# Revit family: Combination_Tissue_Toilet_Seat_Dispenser-Bobrick-ClassicSeries-B-3091
name_source: partatom
category: Specialty Equipment
revit_build: Autodesk Revit 2014 (Build: 20130308_1515(x64)
units: mm (PartAtom-declared; Revit-internal decimal feet)

## types (1)
- B-3091
    ADA Compliant = No
    Assembly Code = C1030200
    Default Elevation = 17 7/8"
    Depth = 3 15/16"
    Description = ClassicSeries Recessed Toilet Seat-Cover Dispenser, Waste Disposal, and Toilet Tissue Dispenser
    Finish = Stainless Steel-Bobrick-Type 304-Satin
    Height = 14"
    Installation Type = Surface-Mounted
    Manufacturer = Bobrick
    Material = Stainless Steel-Bobrick-Type 304-Satin
    Model = B-3091
    Price = Prices may vary. Please consult Manufacturer Representative for most up-to-date price list.
    Revised Date = 08/15/2019
    URL = http://www.bobrick.com
    Width = 28"

## geometry (parser evidence)
native form markers: Sweep x3
no freeform markers — native parametric forms only
